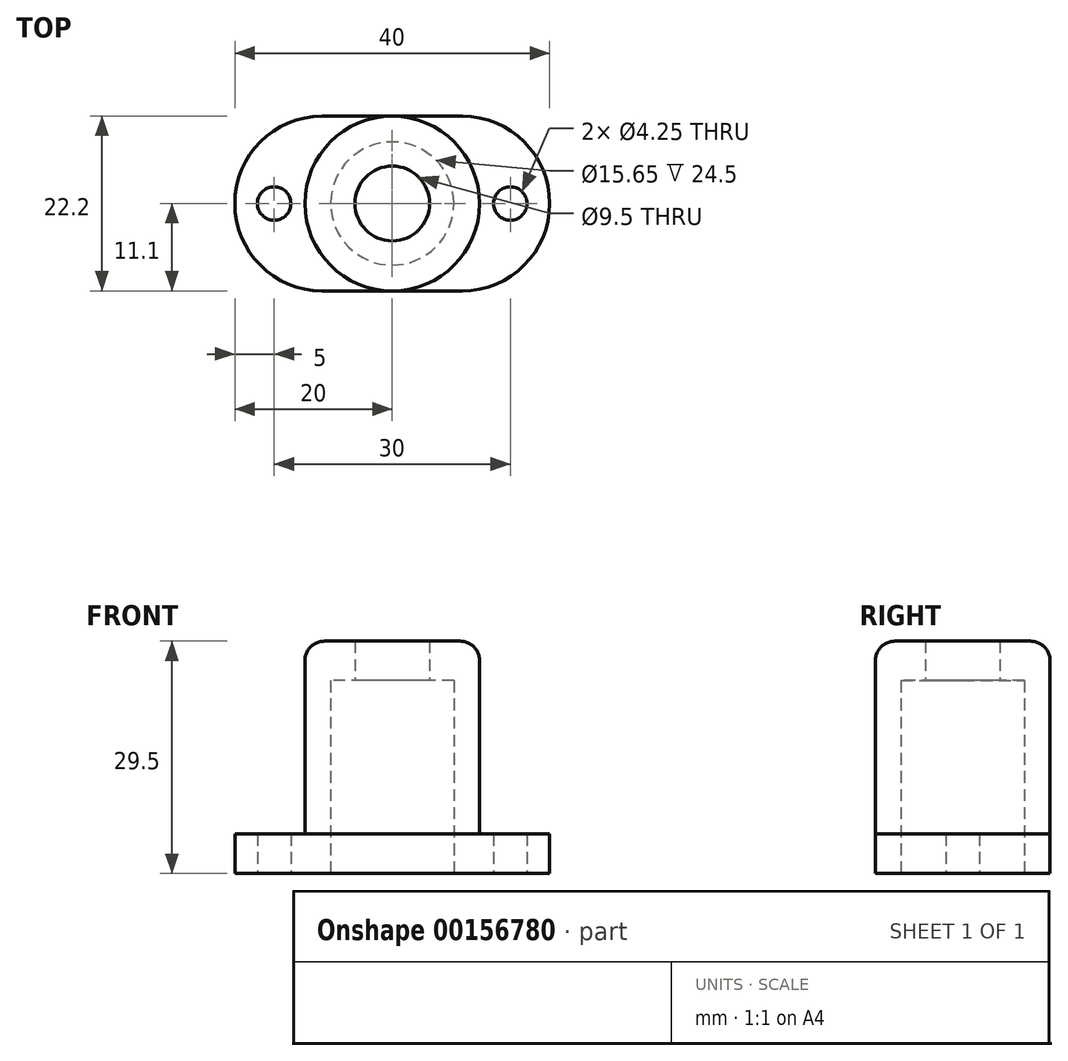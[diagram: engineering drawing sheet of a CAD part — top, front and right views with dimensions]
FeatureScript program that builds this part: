
annotation { "Feature Type Name" : "Feature", "Feature Type Description" : "" }
export const myFeature = defineFeature(function(context is Context, id is Id, definition is map)
    precondition{}
    {
        {
            var Q0;
            Q0=qCreatedBy(makeId("Top.planeOp"),FACE);
            var sketch = newSketch(context, id + "F0", { "sketchPlane" : qUnion([Q0])});
            skCircle(sketch, "E0", {"center": v(0, 0) * mm, "radius": 7.83 * mm});
            skLineSegment(sketch, "E1.bottom", {"start": v(20, -11.1) * mm, "end": v(-20, -11.1) * mm});
            skLineSegment(sketch, "E1.top", {"start": v(20, 11.1) * mm, "end": v(-20, 11.1) * mm});
            skLineSegment(sketch, "E1.left", {"start": v(20, -11.1) * mm, "end": v(20, 11.1) * mm});
            skLineSegment(sketch, "E1.right", {"start": v(-20, -11.1) * mm, "end": v(-20, 11.1) * mm});
            skCircle(sketch, "E2", {"center": v(-15, 0) * mm, "radius": 2.12 * mm});
            skCircle(sketch, "E3.MirrorC", {"center": v(15, 0) * mm, "radius": 2.12 * mm});
            skSolve(sketch);
        }
        {
            var Q0;
            Q0 = qSketchRegion(id + "F0", true);
            extrude(context, id + "F1", {"entities" : qUnion([Q0]), "depth" : 5 * mm});
        }
        {
            var Q0;
            Q0=makeQuery(id+"F1.opExtrude","CAP_FACE",FACE,{"disambiguationData":[OSD([sQuery(id+"F0.wireOp",EDGE,"E0"),sQuery(id+"F0.wireOp",EDGE,"E1.bottom"),sQuery(id+"F0.wireOp",EDGE,"E1.top"),sQuery(id+"F0.wireOp",EDGE,"E1.left"),sQuery(id+"F0.wireOp",EDGE,"E1.right")])],"isStart":false});
            var sketch = newSketch(context, id + "F2", { "sketchPlane" : qUnion([Q0])});
            skCircle(sketch, "E4", {"center": v(0, 0) * mm, "radius": 11.1 * mm});
            skCircle(sketch, "E5", {"center": v(0, 0) * mm, "radius": 7.83 * mm});
            skSolve(sketch);
        }
        {
            var Q0;
            Q0 = qSketchRegion(id + "F2", true);
            extrude(context, id + "F3", {"entities" : qUnion([Q0]), "operationType" : NewBodyOperationType.ADD, "depth" : 19.5 * mm});
        }
        {
            var Q0;
            Q0=makeQuery(id+"F3.opExtrude","CAP_FACE",FACE,{"disambiguationData":[OSD([sQuery(id+"F2.wireOp",EDGE,"E4"),sQuery(id+"F2.wireOp",EDGE,"E5")])],"isStart":false});
            var sketch = newSketch(context, id + "F4", { "sketchPlane" : qUnion([Q0])});
            skCircle(sketch, "E6", {"center": v(0, 0) * mm, "radius": 4.75 * mm});
            skCircle(sketch, "E7", {"center": v(0, 0) * mm, "radius": 11.1 * mm});
            skSolve(sketch);
        }
        {
            var Q0;
            Q0 = qSketchRegion(id + "F4", true);
            extrude(context, id + "F5", {"entities" : qUnion([Q0]), "operationType" : NewBodyOperationType.ADD, "depth" : 5 * mm});
        }
        {
            var Q0;
            Q0=makeQuery(id+"F1.opExtrude","SWEPT_EDGE",EDGE,{"disambiguationData":[OSD([sQuery(id+"F0.wireOp",EDGE,"E1.top"),sQuery(id+"F0.wireOp",EDGE,"E1.right")])]});
            var Q1;
            Q1=makeQuery(id+"F1.opExtrude","SWEPT_EDGE",EDGE,{"disambiguationData":[OSD([sQuery(id+"F0.wireOp",EDGE,"E1.bottom"),sQuery(id+"F0.wireOp",EDGE,"E1.right")])]});
            var Q2;
            Q2=makeQuery(id+"F1.opExtrude","SWEPT_EDGE",EDGE,{"disambiguationData":[OSD([sQuery(id+"F0.wireOp",EDGE,"E1.bottom"),sQuery(id+"F0.wireOp",EDGE,"E1.left")])]});
            var Q3;
            Q3=makeQuery(id+"F1.opExtrude","SWEPT_EDGE",EDGE,{"disambiguationData":[OSD([sQuery(id+"F0.wireOp",EDGE,"E1.top"),sQuery(id+"F0.wireOp",EDGE,"E1.left")])]});
            fillet(context, id + "F6", {"entities" : qUnion([Q0, Q1, Q2, Q3]), "radius" : 11.1 * mm, "tangentPropagation" : true, "allowEdgeOverflow" : false});
        }
        {
            var Q0;
            Q0=makeQuery(id+"F5.opExtrude","CAP_EDGE",EDGE,{"disambiguationData":[OSD([sQuery(id+"F4.wireOp",EDGE,"E7")])],"isStart":false});
            fillet(context, id + "F7", {"entities" : qUnion([Q0]), "radius" : 2.5 * mm, "tangentPropagation" : true, "allowEdgeOverflow" : false});
        }
    });
